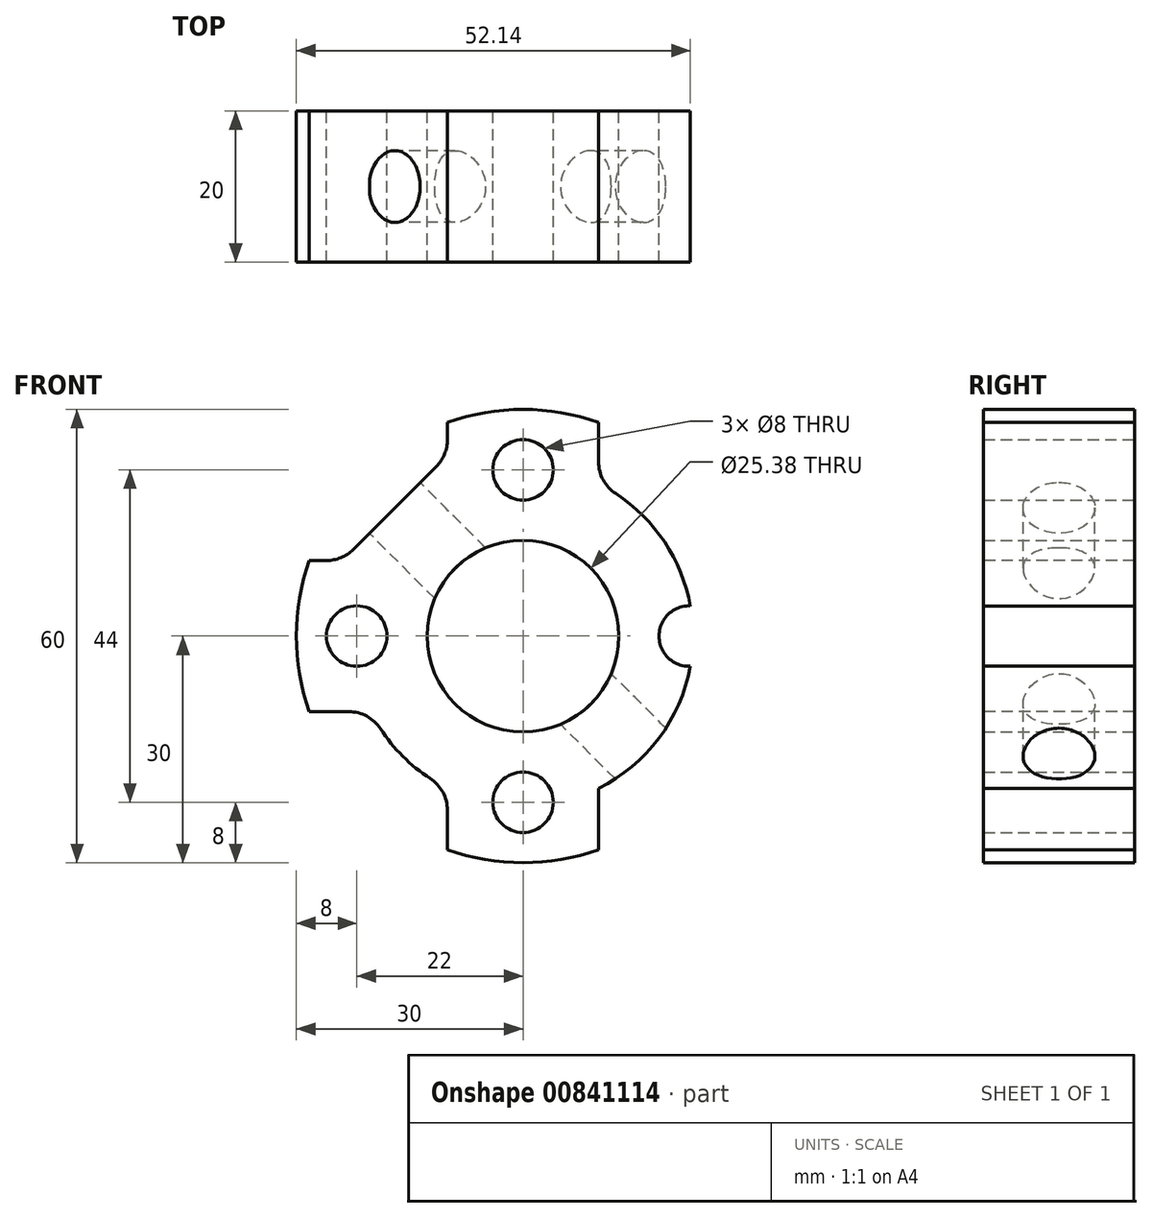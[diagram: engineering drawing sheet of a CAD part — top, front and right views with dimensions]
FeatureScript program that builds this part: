
annotation { "Feature Type Name" : "Feature", "Feature Type Description" : "" }
export const myFeature = defineFeature(function(context is Context, id is Id, definition is map)
    precondition{}
    {
        {
            var Q0;
            Q0=qCreatedBy(makeId("Front.planeOp"),FACE);
            var sketch = newSketch(context, id + "F0", { "sketchPlane" : qUnion([Q0])});
            skCircle(sketch, "E0", {"center": v(0, 0) * mm, "radius": 22.5 * mm});
            skCircle(sketch, "E1", {"center": v(0, 0) * mm, "radius": 12.7 * mm});
            skSolve(sketch);
        }
        {
            var Q0;
            Q0 = qSketchRegion(id + "F0", true);
            extrude(context, id + "F1", {"entities" : qUnion([Q0]), "depth" : 20 * mm, "offsetDistance" : 25 * mm});
        }
        {
            var Q0;
            Q0=qCreatedBy(makeId("Front.planeOp"),FACE);
            var sketch = newSketch(context, id + "F2", { "sketchPlane" : qUnion([Q0])});
            skArc(sketch, "E2", {"start": v(10, 28.28) * mm, "mid": v(0, 30) * mm, "end": v(-10, 28.28) * mm});
            skArc(sketch, "E3", {"start": v(10, 14.36) * mm, "mid": v(0, 17.5) * mm, "end": v(-10, 14.36) * mm});
            skLineSegment(sketch, "E4", {"start": v(-10, 28.28) * mm, "end": v(-10, 14.36) * mm});
            skLineSegment(sketch, "E5.MirrorCS", {"start": v(10, 28.28) * mm, "end": v(10, 14.36) * mm});
            skLineSegment(sketch, "E6", {"start": v(0, 0) * mm, "end": v(28.22, 28.22) * mm, "construction": true});
            skLineSegment(sketch, "E7", {"start": v(0, 0) * mm, "end": v(-31.36, 31.36) * mm, "construction": true});
            skArc(sketch, "E8.MirrorCS", {"start": v(28.28, 10) * mm, "mid": v(30, 0) * mm, "end": v(28.28, -10) * mm});
            skLineSegment(sketch, "E9.MirrorCS", {"start": v(28.28, -10) * mm, "end": v(14.36, -10) * mm});
            skArc(sketch, "E10.MirrorCS", {"start": v(14.36, 10) * mm, "mid": v(17.5, 0) * mm, "end": v(14.36, -10) * mm});
            skLineSegment(sketch, "E11.MirrorCS", {"start": v(28.28, 10) * mm, "end": v(14.36, 10) * mm});
            skLineSegment(sketch, "E12.MirrorCS", {"start": v(-28.28, 10) * mm, "end": v(-14.36, 10) * mm});
            skArc(sketch, "E13.MirrorCS", {"start": v(-28.28, -10) * mm, "mid": v(-30, 0) * mm, "end": v(-28.28, 10) * mm});
            skLineSegment(sketch, "E14.MirrorCS", {"start": v(-28.28, -10) * mm, "end": v(-14.36, -10) * mm});
            skArc(sketch, "E15.MirrorCS", {"start": v(-14.36, -10) * mm, "mid": v(-17.5, 0) * mm, "end": v(-14.36, 10) * mm});
            skLineSegment(sketch, "E16.MirrorCS", {"start": v(-10, -28.28) * mm, "end": v(-10, -14.36) * mm});
            skArc(sketch, "E17.MirrorCS", {"start": v(-10, -14.36) * mm, "mid": v(0, -17.5) * mm, "end": v(10, -14.36) * mm});
            skLineSegment(sketch, "E18.MirrorCS", {"start": v(10, -28.28) * mm, "end": v(10, -14.36) * mm});
            skArc(sketch, "E19.MirrorCS", {"start": v(-10, -28.28) * mm, "mid": v(0, -30) * mm, "end": v(10, -28.28) * mm});
            skSolve(sketch);
        }
        {
            var Q0;
            Q0=makeQuery(id+"F2.imprint","IMPRINT",FACE,{"disambiguationData":[TD([[makeQuery(id+"F2.imprint","IMPRINT",EDGE,{"derivedFrom":sQuery(id+"F2.wireOp",EDGE,"E2")}),1.0]])]});
            var Q1;
            Q1=makeQuery(id+"F2.imprint","IMPRINT",FACE,{"disambiguationData":[TD([[makeQuery(id+"F2.imprint","IMPRINT",EDGE,{"derivedFrom":sQuery(id+"F2.wireOp",EDGE,"E12.MirrorCS")}),-1.0]])]});
            var Q2;
            Q2=makeQuery(id+"F2.imprint","IMPRINT",FACE,{"disambiguationData":[TD([[makeQuery(id+"F2.imprint","IMPRINT",EDGE,{"derivedFrom":sQuery(id+"F2.wireOp",EDGE,"E8.MirrorCS")}),-1.0]])]});
            var Q3;
            Q3=makeQuery(id+"F2.imprint","IMPRINT",FACE,{"disambiguationData":[TD([[makeQuery(id+"F2.imprint","IMPRINT",EDGE,{"derivedFrom":sQuery(id+"F2.wireOp",EDGE,"E16.MirrorCS")}),-1.0]])]});
            extrude(context, id + "F3", {"entities" : qUnion([Q0, Q1, Q2, Q3]), "operationType" : NewBodyOperationType.ADD, "depth" : 20 * mm, "offsetDistance" : 25 * mm});
        }
        {
            var Q0;
            Q0=qCreatedBy(makeId("Front.planeOp"),FACE);
            var sketch = newSketch(context, id + "F4", { "sketchPlane" : qUnion([Q0])});
            skCircle(sketch, "E20", {"center": v(4, 21) * mm, "radius": 2.5 * mm});
            skCircle(sketch, "E21.MirrorC", {"center": v(-4, 21) * mm, "radius": 2.5 * mm});
            skCircle(sketch, "E22.MirrorC", {"center": v(-4, -21) * mm, "radius": 2.5 * mm});
            skCircle(sketch, "E23.MirrorC", {"center": v(4, -21) * mm, "radius": 2.5 * mm});
            skSolve(sketch);
        }
        {
            var Q0;
            Q0=qCreatedBy(makeId("Front.planeOp"),FACE);
            var sketch = newSketch(context, id + "F5", { "sketchPlane" : qUnion([Q0])});
            skCircle(sketch, "E24", {"center": v(0, 22) * mm, "radius": 4 * mm});
            skCircle(sketch, "E25.MirrorC", {"center": v(0, -22) * mm, "radius": 4 * mm});
            skLineSegment(sketch, "E26", {"start": v(0, 0) * mm, "end": v(27.06, 27.06) * mm, "construction": true});
            skCircle(sketch, "E27.MirrorC", {"center": v(22, 0) * mm, "radius": 4 * mm});
            skCircle(sketch, "E28.MirrorC", {"center": v(-22, 0) * mm, "radius": 4 * mm});
            skSolve(sketch);
        }
        {
            var Q0;
            Q0 = qSketchRegion(id + "F5", true);
            extrude(context, id + "F6", {"entities" : qUnion([Q0]), "operationType" : NewBodyOperationType.REMOVE, "depth" : 52.7 * mm, "offsetDistance" : 25 * mm});
        }
        {
            var Q0;
            Q0=qCreatedBy(makeId("Front.planeOp"),FACE);
            var sketch = newSketch(context, id + "F7", { "sketchPlane" : qUnion([Q0])});
            skLineSegment(sketch, "E29", {"start": v(-26.94, 7) * mm, "end": v(-7, 26.94) * mm});
            skLineSegment(sketch, "E30", {"start": v(0, 0) * mm, "end": v(-27.69, 27.69) * mm, "construction": true});
            skArc(sketch, "E31", {"start": v(-7, 13.27) * mm, "mid": v(-10.6, 10.6) * mm, "end": v(-13.27, 7) * mm});
            skLineSegment(sketch, "E32", {"start": v(-7, 26.94) * mm, "end": v(-7, 13.27) * mm});
            skLineSegment(sketch, "E33", {"start": v(-26.94, 7) * mm, "end": v(-13.27, 7) * mm});
            skLineSegment(sketch, "E34", {"start": v(0, 0) * mm, "end": v(27.85, 27.85) * mm, "construction": true});
            skLineSegment(sketch, "E35.MirrorCS", {"start": v(0, 0) * mm, "end": v(27.69, -27.69) * mm, "construction": true});
            skArc(sketch, "E36.MirrorCS", {"start": v(13.27, -7) * mm, "mid": v(10.6, -10.6) * mm, "end": v(7, -13.27) * mm});
            skLineSegment(sketch, "E37.MirrorCS", {"start": v(26.94, -7) * mm, "end": v(13.27, -7) * mm});
            skLineSegment(sketch, "E38.MirrorCS", {"start": v(7, -26.94) * mm, "end": v(7, -13.27) * mm});
            skLineSegment(sketch, "E39.MirrorCS", {"start": v(7, -26.94) * mm, "end": v(26.94, -7) * mm});
            skSolve(sketch);
        }
        {
            var Q0;
            Q0=makeQuery(id+"F7.imprint","IMPRINT",FACE,{"disambiguationData":[TD([[makeQuery(id+"F7.imprint","IMPRINT",EDGE,{"derivedFrom":sQuery(id+"F7.wireOp",EDGE,"E29")}),-1.0]])]});
            var Q1;
            Q1=makeQuery(id+"F7.imprint","IMPRINT",FACE,{"disambiguationData":[TD([[makeQuery(id+"F7.imprint","IMPRINT",EDGE,{"derivedFrom":sQuery(id+"F7.wireOp",EDGE,"E36.MirrorCS")}),1.0]])]});
            extrude(context, id + "F8", {"entities" : qUnion([Q0, Q1]), "operationType" : NewBodyOperationType.ADD, "depth" : 20 * mm, "offsetDistance" : 25 * mm});
        }
        {
            var Q0;
            Q0=makeQuery(id+"F3.boolean.opBoolean","INTERSECT",EDGE,{"derivedFrom":[makeQuery(id+"F1.opExtrude","SWEPT_FACE",FACE,{"disambiguationData":[OSD([sQuery(id+"F0.wireOp",EDGE,"E0")])]}),makeQuery(id+"F3.opExtrude","SWEPT_FACE",FACE,{"disambiguationData":[OSD([sQuery(id+"F2.wireOp",EDGE,"E5.MirrorCS")])]})]});
            var Q1;
            Q1=makeQuery(id+"F3.boolean.opBoolean","INTERSECT",EDGE,{"derivedFrom":[makeQuery(id+"F1.opExtrude","SWEPT_FACE",FACE,{"disambiguationData":[OSD([sQuery(id+"F0.wireOp",EDGE,"E0")])]}),makeQuery(id+"F3.opExtrude","SWEPT_FACE",FACE,{"disambiguationData":[OSD([sQuery(id+"F2.wireOp",EDGE,"E11.MirrorCS")])]})]});
            var Q2;
            Q2=makeQuery(id+"F3.boolean.opBoolean","INTERSECT",EDGE,{"derivedFrom":[makeQuery(id+"F1.opExtrude","SWEPT_FACE",FACE,{"disambiguationData":[OSD([sQuery(id+"F0.wireOp",EDGE,"E0")])]}),makeQuery(id+"F3.opExtrude","SWEPT_FACE",FACE,{"disambiguationData":[OSD([sQuery(id+"F2.wireOp",EDGE,"E16.MirrorCS")])]})]});
            var Q3;
            Q3=makeQuery(id+"F3.boolean.opBoolean","INTERSECT",EDGE,{"derivedFrom":[makeQuery(id+"F1.opExtrude","SWEPT_FACE",FACE,{"disambiguationData":[OSD([sQuery(id+"F0.wireOp",EDGE,"E0")])]}),makeQuery(id+"F3.opExtrude","SWEPT_FACE",FACE,{"disambiguationData":[OSD([sQuery(id+"F2.wireOp",EDGE,"E14.MirrorCS")])]})]});
            var Q4;
            Q4=makeQuery(id+"F8.boolean.opBoolean","INTERSECT",EDGE,{"derivedFrom":[makeQuery(id+"F3.opExtrude","SWEPT_FACE",FACE,{"disambiguationData":[OSD([sQuery(id+"F2.wireOp",EDGE,"E4")])]}),makeQuery(id+"F8.opExtrude","SWEPT_FACE",FACE,{"disambiguationData":[OSD([sQuery(id+"F7.wireOp",EDGE,"E29")])]})]});
            var Q5;
            Q5=makeQuery(id+"F8.boolean.opBoolean","INTERSECT",EDGE,{"derivedFrom":[makeQuery(id+"F3.opExtrude","SWEPT_FACE",FACE,{"disambiguationData":[OSD([sQuery(id+"F2.wireOp",EDGE,"E12.MirrorCS")])]}),makeQuery(id+"F8.opExtrude","SWEPT_FACE",FACE,{"disambiguationData":[OSD([sQuery(id+"F7.wireOp",EDGE,"E29")])]})]});
            var Q6;
            Q6=makeQuery(id+"F8.boolean.opBoolean","INTERSECT",EDGE,{"derivedFrom":[makeQuery(id+"F3.opExtrude","SWEPT_FACE",FACE,{"disambiguationData":[OSD([sQuery(id+"F2.wireOp",EDGE,"E9.MirrorCS")])]}),makeQuery(id+"F8.opExtrude","SWEPT_FACE",FACE,{"disambiguationData":[OSD([sQuery(id+"F7.wireOp",EDGE,"E39.MirrorCS")])]})]});
            var Q7;
            Q7=makeQuery(id+"F8.boolean.opBoolean","INTERSECT",EDGE,{"derivedFrom":[makeQuery(id+"F3.opExtrude","SWEPT_FACE",FACE,{"disambiguationData":[OSD([sQuery(id+"F2.wireOp",EDGE,"E18.MirrorCS")])]}),makeQuery(id+"F8.opExtrude","SWEPT_FACE",FACE,{"disambiguationData":[OSD([sQuery(id+"F7.wireOp",EDGE,"E39.MirrorCS")])]})]});
            fillet(context, id + "F9", {"entities" : qUnion([Q0, Q1, Q2, Q3, Q4, Q5, Q6, Q7]), "radius" : 5 * mm, "tangentPropagation" : true, "allowEdgeOverflow" : false});
        }
        {
            var Q0;
            Q0=makeQuery(id+"F8.opExtrude","SWEPT_FACE",FACE,{"disambiguationData":[OSD([sQuery(id+"F7.wireOp",EDGE,"E29")])]});
            var sketch = newSketch(context, id + "F10", { "sketchPlane" : qUnion([Q0])});
            skCircle(sketch, "E40", {"center": v(10, 0) * mm, "radius": 4.75 * mm});
            skSolve(sketch);
        }
        {
            var Q0;
            Q0 = qSketchRegion(id + "F10", true);
            extrude(context, id + "F11", {"entities" : qUnion([Q0]), "operationType" : NewBodyOperationType.REMOVE, "endBound" : BoundingType.SYMMETRIC, "oppositeDirection" : true, "depth" : 111.6 * mm, "offsetDistance" : 25 * mm});
        }
    });
